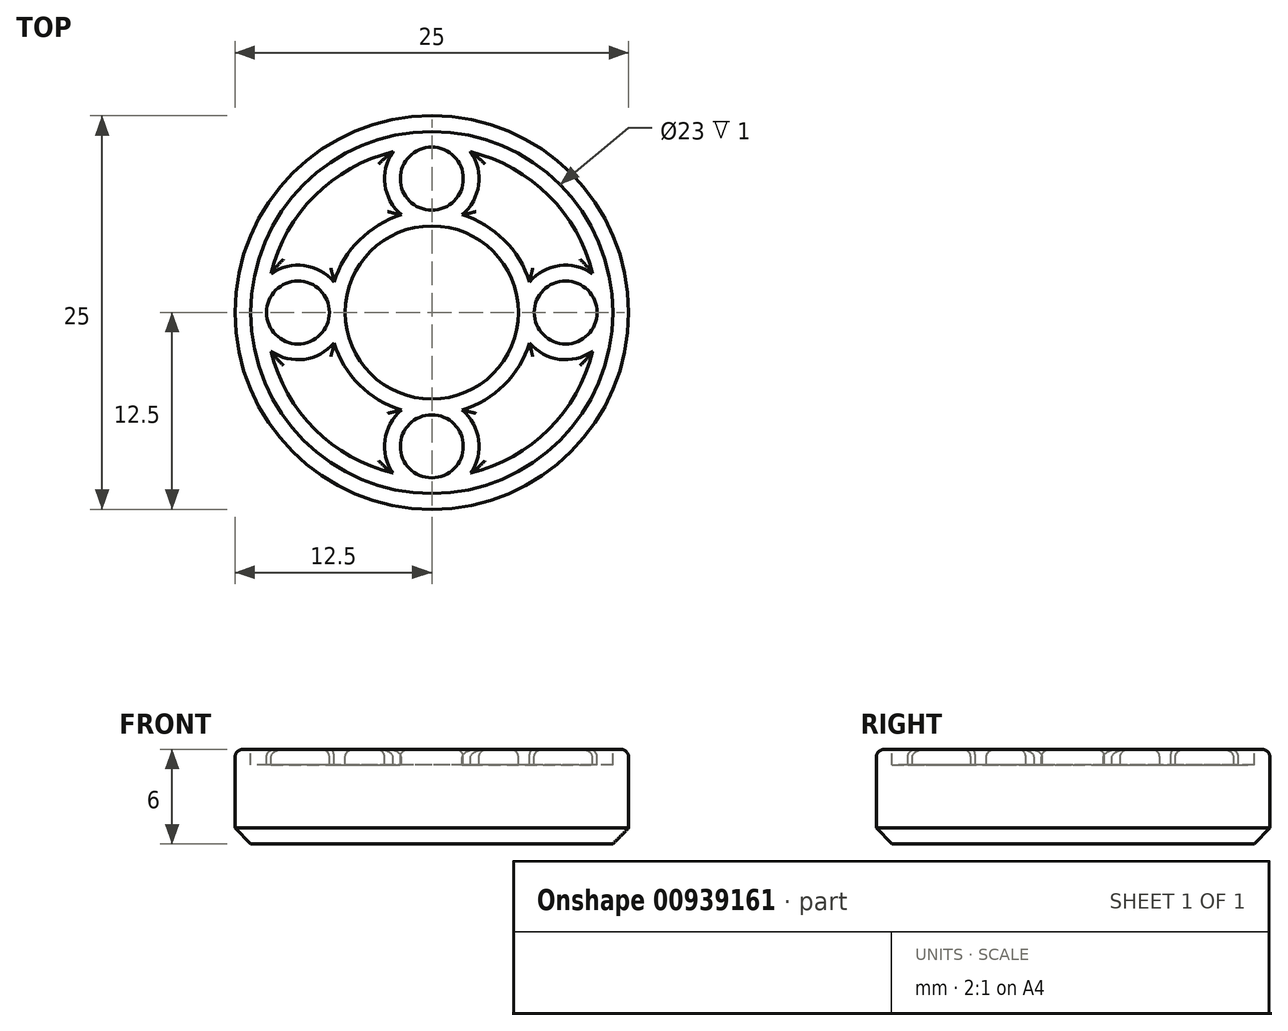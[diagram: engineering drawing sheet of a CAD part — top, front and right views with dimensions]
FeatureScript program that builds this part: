
annotation { "Feature Type Name" : "Feature", "Feature Type Description" : "" }
export const myFeature = defineFeature(function(context is Context, id is Id, definition is map)
    precondition{}
    {
        {
            var Q0;
            Q0=qCreatedBy(makeId("Top.planeOp"),FACE);
            var sketch = newSketch(context, id + "F0", { "sketchPlane" : qUnion([Q0])});
            skCircle(sketch, "E0", {"center": v(0, 0) * mm, "radius": 12.5 * mm});
            skSolve(sketch);
        }
        {
            var Q0;
            Q0 = qSketchRegion(id + "F0", true);
            extrude(context, id + "F1", {"entities" : qUnion([Q0]), "depth" : 6 * mm, "offsetDistance" : 25 * mm});
        }
        {
            var Q0;
            Q0=makeQuery(id+"F1.opExtrude","CAP_FACE",FACE,{"disambiguationData":[OSD([sQuery(id+"F0.wireOp",EDGE,"E0")])],"isStart":false});
            var sketch = newSketch(context, id + "F2", { "sketchPlane" : qUnion([Q0])});
            skCircle(sketch, "E1", {"center": v(0, 0) * mm, "radius": 11.5 * mm});
            skArc(sketch, "E2", {"start": v(-2.47, 10.2) * mm, "mid": v(-7.42, 7.42) * mm, "end": v(-10.2, 2.47) * mm});
            skLineSegment(sketch, "E3", {"start": v(0, 10.5) * mm, "end": v(0, 8.5) * mm, "construction": true});
            skArc(sketch, "E4", {"start": v(-2.47, 10.2) * mm, "mid": v(-2.97, 8.1) * mm, "end": v(-1.93, 6.2) * mm});
            skCircle(sketch, "E5", {"center": v(0, 8.5) * mm, "radius": 2 * mm});
            skArc(sketch, "E6", {"start": v(-1.93, 6.2) * mm, "mid": v(-4.6, 4.6) * mm, "end": v(-6.2, 1.93) * mm});
            skLineSegment(sketch, "E7", {"start": v(-10.5, 0) * mm, "end": v(-8.5, 0) * mm, "construction": true});
            skLineSegment(sketch, "E8", {"start": v(10.5, 0) * mm, "end": v(8.5, 0) * mm, "construction": true});
            skLineSegment(sketch, "E9", {"start": v(0, -10.5) * mm, "end": v(0, -8.5) * mm, "construction": true});
            skArc(sketch, "E10", {"start": v(-6.2, 1.93) * mm, "mid": v(-8.1, 2.97) * mm, "end": v(-10.2, 2.47) * mm});
            skCircle(sketch, "E11", {"center": v(-8.5, 0) * mm, "radius": 2 * mm});
            skArc(sketch, "E12", {"start": v(2.47, -10.2) * mm, "mid": v(2.97, -8.1) * mm, "end": v(1.93, -6.2) * mm});
            skCircle(sketch, "E13", {"center": v(0, -8.5) * mm, "radius": 2 * mm});
            skArc(sketch, "E14", {"start": v(10.2, 2.47) * mm, "mid": v(8.1, 2.97) * mm, "end": v(6.2, 1.93) * mm});
            skCircle(sketch, "E15", {"center": v(8.5, 0) * mm, "radius": 2 * mm});
            skCircle(sketch, "E16", {"center": v(0, 0) * mm, "radius": 5.5 * mm});
            skArc(sketch, "E17.trimOffspring", {"start": v(1.93, 6.2) * mm, "mid": v(2.97, 8.1) * mm, "end": v(2.47, 10.2) * mm});
            skArc(sketch, "E18.trimOffspring", {"start": v(-6.2, -1.93) * mm, "mid": v(-4.6, -4.6) * mm, "end": v(-1.93, -6.2) * mm});
            skArc(sketch, "E19.trimOffspring", {"start": v(-10.2, -2.47) * mm, "mid": v(-7.42, -7.42) * mm, "end": v(-2.47, -10.2) * mm});
            skArc(sketch, "E20.trimOffspring", {"start": v(-10.2, -2.47) * mm, "mid": v(-8.1, -2.97) * mm, "end": v(-6.2, -1.93) * mm});
            skArc(sketch, "E21.trimOffspring", {"start": v(2.47, -10.2) * mm, "mid": v(7.42, -7.42) * mm, "end": v(10.2, -2.47) * mm});
            skArc(sketch, "E22.trimOffspring", {"start": v(1.93, -6.2) * mm, "mid": v(4.6, -4.6) * mm, "end": v(6.2, -1.93) * mm});
            skArc(sketch, "E23.trimOffspring", {"start": v(-1.93, -6.2) * mm, "mid": v(-2.97, -8.1) * mm, "end": v(-2.47, -10.2) * mm});
            skArc(sketch, "E24.trimOffspring", {"start": v(6.2, 1.93) * mm, "mid": v(4.6, 4.6) * mm, "end": v(1.93, 6.2) * mm});
            skArc(sketch, "E25.trimOffspring", {"start": v(10.2, 2.47) * mm, "mid": v(7.42, 7.42) * mm, "end": v(2.47, 10.2) * mm});
            skArc(sketch, "E26.trimOffspring", {"start": v(6.2, -1.93) * mm, "mid": v(8.1, -2.97) * mm, "end": v(10.2, -2.47) * mm});
            skSolve(sketch);
        }
        {
            var Q0;
            Q0 = qSketchRegion(id + "F2", true);
            extrude(context, id + "F3", {"entities" : qUnion([Q0]), "operationType" : NewBodyOperationType.REMOVE, "oppositeDirection" : true, "depth" : 1 * mm, "offsetDistance" : 25 * mm});
        }
        {
            var Q0;
            Q0=makeQuery(id+"F1.opExtrude","CAP_EDGE",EDGE,{"disambiguationData":[OSD([sQuery(id+"F0.wireOp",EDGE,"E0")])],"isStart":true});
            chamfer(context, id + "F4", {"entities" : qUnion([Q0]), "width" : 1 * mm, "tangentPropagation" : true});
        }
        {
            var Q0;
            Q0=makeQuery(id+"F1.opExtrude","CAP_EDGE",EDGE,{"disambiguationData":[OSD([sQuery(id+"F0.wireOp",EDGE,"E0")])],"isStart":false});
            var Q1;
            Q1=makeQuery(id+"F3.boolean.opBoolean","COPY",EDGE,{"derivedFrom":makeQuery(id+"F3.opExtrude","CAP_EDGE",EDGE,{"disambiguationData":[OSD([sQuery(id+"F2.wireOp",EDGE,"E1")])],"isStart":true})});
            var Q2;
            Q2=makeQuery(id+"F3.boolean.opBoolean","SPLIT",FACE,{"disambiguationData":[TD([makeQuery(id+"F3.opExtrude","SWEPT_FACE",FACE,{"disambiguationData":[OSD([sQuery(id+"F2.wireOp",EDGE,"E2")])]})])],"derivedFrom":makeQuery(id+"F1.opExtrude","CAP_FACE",FACE,{"disambiguationData":[OSD([sQuery(id+"F0.wireOp",EDGE,"E0")])],"isStart":false})});
            var Q3;
            Q3=makeQuery(id+"F3.boolean.opBoolean","SPLIT",FACE,{"disambiguationData":[TD([makeQuery(id+"F3.opExtrude","SWEPT_FACE",FACE,{"disambiguationData":[OSD([sQuery(id+"F2.wireOp",EDGE,"E11")])]})])],"derivedFrom":makeQuery(id+"F1.opExtrude","CAP_FACE",FACE,{"disambiguationData":[OSD([sQuery(id+"F0.wireOp",EDGE,"E0")])],"isStart":false})});
            var Q4;
            Q4=makeQuery(id+"F3.boolean.opBoolean","SPLIT",FACE,{"disambiguationData":[TD([makeQuery(id+"F3.opExtrude","SWEPT_FACE",FACE,{"disambiguationData":[OSD([sQuery(id+"F2.wireOp",EDGE,"E18.trimOffspring")])]})])],"derivedFrom":makeQuery(id+"F1.opExtrude","CAP_FACE",FACE,{"disambiguationData":[OSD([sQuery(id+"F0.wireOp",EDGE,"E0")])],"isStart":false})});
            var Q5;
            Q5=makeQuery(id+"F3.boolean.opBoolean","SPLIT",FACE,{"disambiguationData":[TD([makeQuery(id+"F3.opExtrude","SWEPT_FACE",FACE,{"disambiguationData":[OSD([sQuery(id+"F2.wireOp",EDGE,"E13")])]})])],"derivedFrom":makeQuery(id+"F1.opExtrude","CAP_FACE",FACE,{"disambiguationData":[OSD([sQuery(id+"F0.wireOp",EDGE,"E0")])],"isStart":false})});
            var Q6;
            Q6=makeQuery(id+"F3.boolean.opBoolean","SPLIT",FACE,{"disambiguationData":[TD([makeQuery(id+"F3.opExtrude","SWEPT_FACE",FACE,{"disambiguationData":[OSD([sQuery(id+"F2.wireOp",EDGE,"E12")])]})])],"derivedFrom":makeQuery(id+"F1.opExtrude","CAP_FACE",FACE,{"disambiguationData":[OSD([sQuery(id+"F0.wireOp",EDGE,"E0")])],"isStart":false})});
            var Q7;
            Q7=makeQuery(id+"F3.boolean.opBoolean","SPLIT",FACE,{"disambiguationData":[TD([makeQuery(id+"F3.opExtrude","SWEPT_FACE",FACE,{"disambiguationData":[OSD([sQuery(id+"F2.wireOp",EDGE,"E15")])]})])],"derivedFrom":makeQuery(id+"F1.opExtrude","CAP_FACE",FACE,{"disambiguationData":[OSD([sQuery(id+"F0.wireOp",EDGE,"E0")])],"isStart":false})});
            var Q8;
            Q8=makeQuery(id+"F3.boolean.opBoolean","SPLIT",FACE,{"disambiguationData":[TD([makeQuery(id+"F3.opExtrude","SWEPT_FACE",FACE,{"disambiguationData":[OSD([sQuery(id+"F2.wireOp",EDGE,"E14")])]})])],"derivedFrom":makeQuery(id+"F1.opExtrude","CAP_FACE",FACE,{"disambiguationData":[OSD([sQuery(id+"F0.wireOp",EDGE,"E0")])],"isStart":false})});
            var Q9;
            Q9=makeQuery(id+"F3.boolean.opBoolean","SPLIT",FACE,{"disambiguationData":[TD([makeQuery(id+"F3.opExtrude","SWEPT_FACE",FACE,{"disambiguationData":[OSD([sQuery(id+"F2.wireOp",EDGE,"E5")])]})])],"derivedFrom":makeQuery(id+"F1.opExtrude","CAP_FACE",FACE,{"disambiguationData":[OSD([sQuery(id+"F0.wireOp",EDGE,"E0")])],"isStart":false})});
            var Q10;
            Q10=makeQuery(id+"F3.boolean.opBoolean","SPLIT",FACE,{"disambiguationData":[TD([makeQuery(id+"F3.opExtrude","SWEPT_FACE",FACE,{"disambiguationData":[OSD([sQuery(id+"F2.wireOp",EDGE,"E16")])]})])],"derivedFrom":makeQuery(id+"F1.opExtrude","CAP_FACE",FACE,{"disambiguationData":[OSD([sQuery(id+"F0.wireOp",EDGE,"E0")])],"isStart":false})});
            fillet(context, id + "F5", {"entities" : qUnion([Q0, Q1, Q2, Q3, Q4, Q5, Q6, Q7, Q8, Q9, Q10]), "radius" : .5 * mm, "tangentPropagation" : true, "allowEdgeOverflow" : false});
        }
    });
